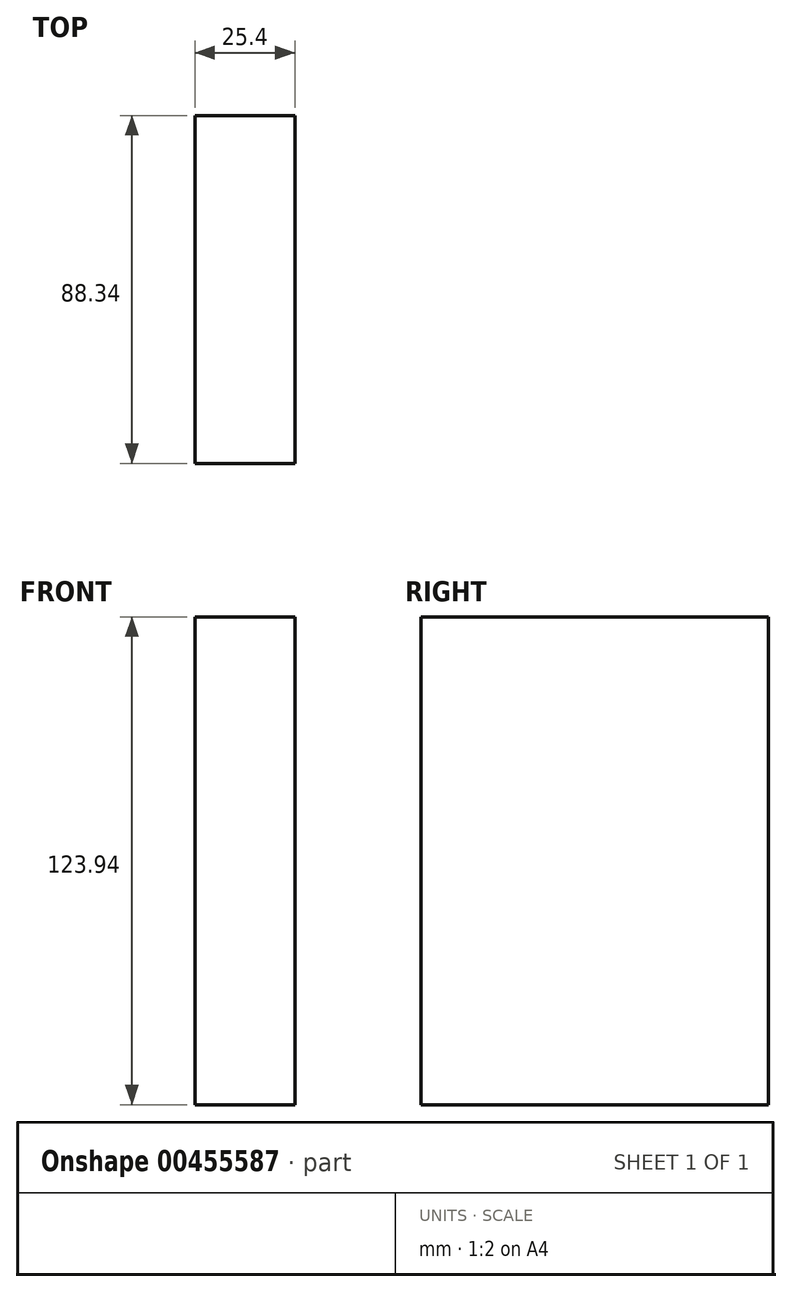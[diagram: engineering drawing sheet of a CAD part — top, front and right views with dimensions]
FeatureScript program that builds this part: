
annotation { "Feature Type Name" : "Feature", "Feature Type Description" : "" }
export const myFeature = defineFeature(function(context is Context, id is Id, definition is map)
    precondition{}
    {
        {
            var Q0;
            Q0=qCreatedBy(makeId("Right.planeOp"),FACE);
            var sketch = newSketch(context, id + "F0", { "sketchPlane" : qUnion([Q0])});
            skLineSegment(sketch, "E0.bottom", {"start": v(-44.17, 61.97) * mm, "end": v(44.17, 61.97) * mm});
            skLineSegment(sketch, "E0.top", {"start": v(-44.17, -61.97) * mm, "end": v(44.17, -61.97) * mm});
            skLineSegment(sketch, "E0.left", {"start": v(-44.17, 61.97) * mm, "end": v(-44.17, -61.97) * mm});
            skLineSegment(sketch, "E0.right", {"start": v(44.17, 61.97) * mm, "end": v(44.17, -61.97) * mm});
            skPoint(sketch, "E0.middle", {"position": v(0, 0) * mm});
            skSolve(sketch);
        }
        {
            var Q0;
            Q0 = qSketchRegion(id + "F0", true);
            extrude(context, id + "F1", {"entities" : qUnion([Q0]), "depth" : 25.4 * mm});
        }
    });
